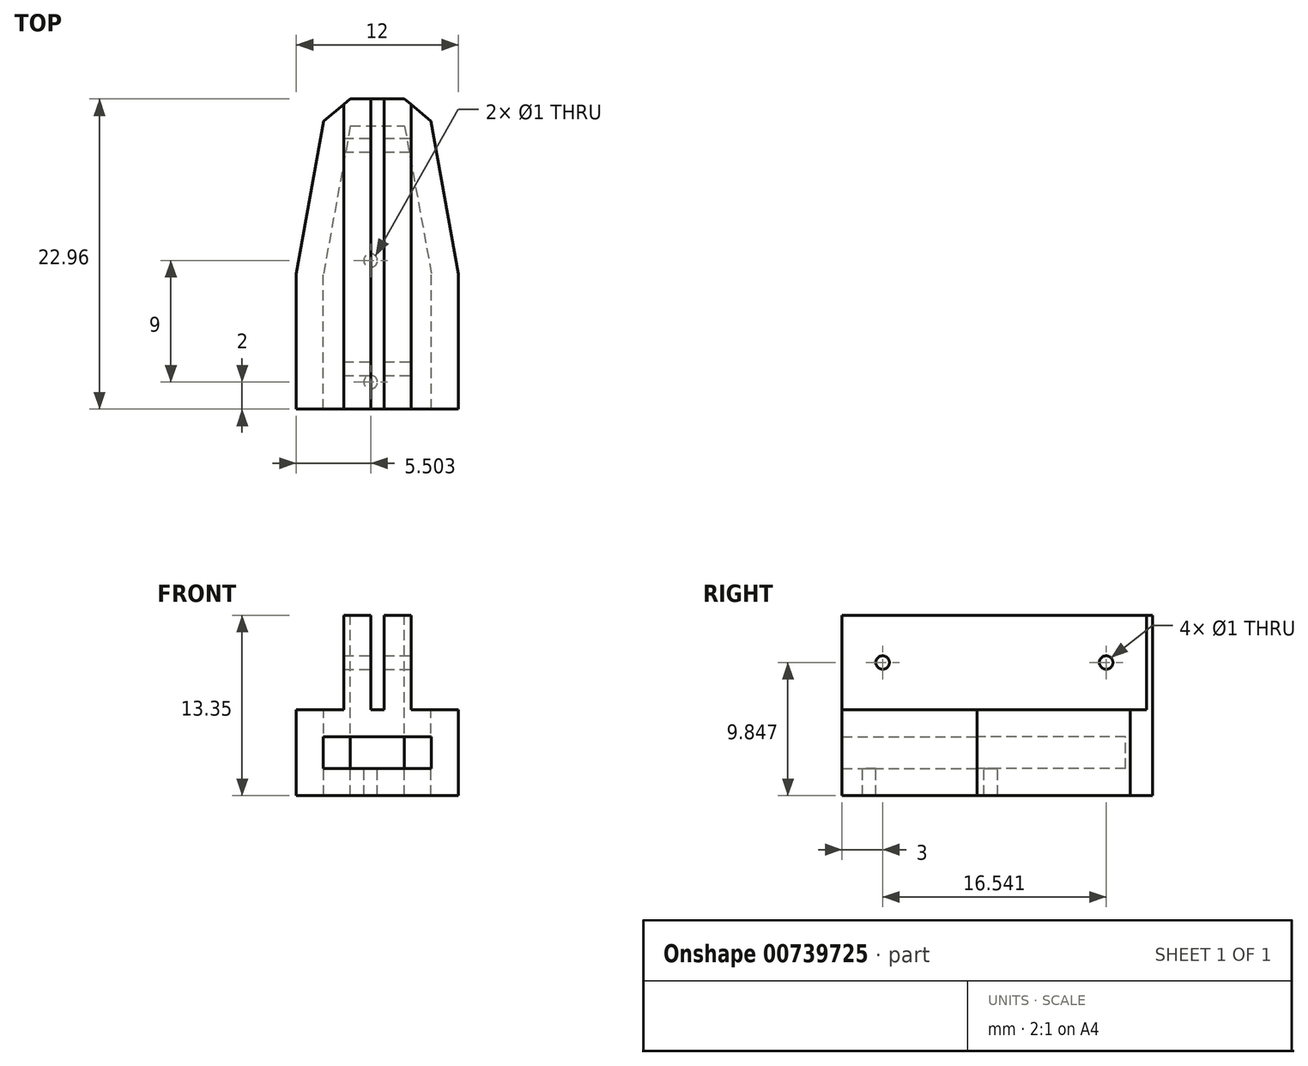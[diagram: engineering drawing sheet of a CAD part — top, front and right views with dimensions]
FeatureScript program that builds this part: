
annotation { "Feature Type Name" : "Feature", "Feature Type Description" : "" }
export const myFeature = defineFeature(function(context is Context, id is Id, definition is map)
    precondition{}
    {
        {
            var Q0;
            Q0=qCreatedBy(makeId("Top.planeOp"),FACE);
            var sketch = newSketch(context, id + "F0", { "sketchPlane" : qUnion([Q0])});
            skLineSegment(sketch, "E0", {"start": v(-17.89, 0) * mm, "end": v(-9.89, 0) * mm});
            skLineSegment(sketch, "E1", {"start": v(-17.89, 0) * mm, "end": v(-17.89, 10) * mm});
            skLineSegment(sketch, "E2", {"start": v(-9.89, 0) * mm, "end": v(-9.89, 10) * mm});
            skLineSegment(sketch, "E3", {"start": v(-11.89, 20.96) * mm, "end": v(-9.89, 10) * mm});
            skLineSegment(sketch, "E4", {"start": v(-15.89, 20.96) * mm, "end": v(-11.89, 20.96) * mm});
            skLineSegment(sketch, "E5", {"start": v(-15.89, 20.96) * mm, "end": v(-17.89, 10) * mm});
            skLineSegment(sketch, "E6", {"start": v(-17.89, 0) * mm, "end": v(-19.89, 0) * mm});
            skLineSegment(sketch, "E7", {"start": v(-17.89, 10) * mm, "end": v(-19.89, 10) * mm});
            skLineSegment(sketch, "E8", {"start": v(-15.89, 20.96) * mm, "end": v(-17.86, 21.32) * mm});
            skLineSegment(sketch, "E9", {"start": v(-11.89, 20.96) * mm, "end": v(-11.89, 22.96) * mm});
            skLineSegment(sketch, "E10", {"start": v(-11.89, 20.96) * mm, "end": v(-9.92, 21.32) * mm});
            skLineSegment(sketch, "E11", {"start": v(-9.89, 0) * mm, "end": v(-7.89, 0) * mm});
            skLineSegment(sketch, "E12", {"start": v(-15.89, 20.96) * mm, "end": v(-15.89, 22.96) * mm});
            skLineSegment(sketch, "E13", {"start": v(-9.89, 10) * mm, "end": v(-7.89, 10) * mm});
            skLineSegment(sketch, "E14", {"start": v(-19.89, 10) * mm, "end": v(-19.89, 0) * mm});
            skLineSegment(sketch, "E15", {"start": v(-17.86, 21.32) * mm, "end": v(-19.89, 10) * mm});
            skLineSegment(sketch, "E16", {"start": v(-17.86, 21.32) * mm, "end": v(-15.89, 22.96) * mm});
            skLineSegment(sketch, "E17", {"start": v(-11.89, 22.96) * mm, "end": v(-15.89, 22.96) * mm});
            skLineSegment(sketch, "E18", {"start": v(-11.89, 22.96) * mm, "end": v(-9.92, 21.32) * mm});
            skLineSegment(sketch, "E19", {"start": v(-9.92, 21.32) * mm, "end": v(-7.89, 10) * mm});
            skLineSegment(sketch, "E20", {"start": v(-7.89, 10) * mm, "end": v(-7.89, 0) * mm});
            skLineSegment(sketch, "E21", {"start": v(-13.89, 20.96) * mm, "end": v(-13.89, 0) * mm});
            skSolve(sketch);
        }
        {
            var Q0;
            Q0=makeQuery(id+"F0.imprint","IMPRINT",FACE,{"disambiguationData":[TD([[makeQuery(id+"F0.imprint","IMPRINT",EDGE,{"derivedFrom":sQuery(id+"F0.wireOp",EDGE,"E1")}),1.0]])]});
            var Q1;
            Q1=makeQuery(id+"F0.imprint","IMPRINT",FACE,{"disambiguationData":[TD([[makeQuery(id+"F0.imprint","IMPRINT",EDGE,{"derivedFrom":sQuery(id+"F0.wireOp",EDGE,"E2")}),-1.0]])]});
            var Q2;
            Q2=makeQuery(id+"F0.imprint","IMPRINT",FACE,{"disambiguationData":[TD([[makeQuery(id+"F0.imprint","IMPRINT",EDGE,{"derivedFrom":sQuery(id+"F0.wireOp",EDGE,"E8")}),-1.0]])]});
            var Q3;
            Q3=makeQuery(id+"F0.imprint","IMPRINT",FACE,{"disambiguationData":[TD([[makeQuery(id+"F0.imprint","IMPRINT",EDGE,{"derivedFrom":sQuery(id+"F0.wireOp",EDGE,"E9")}),-1.0]])]});
            var Q4;
            Q4=makeQuery(id+"F0.imprint","IMPRINT",FACE,{"disambiguationData":[TD([[makeQuery(id+"F0.imprint","IMPRINT",EDGE,{"derivedFrom":sQuery(id+"F0.wireOp",EDGE,"E3")}),1.0]])]});
            var Q5;
            Q5=makeQuery(id+"F0.imprint","IMPRINT",FACE,{"disambiguationData":[TD([[makeQuery(id+"F0.imprint","IMPRINT",EDGE,{"derivedFrom":sQuery(id+"F0.wireOp",EDGE,"E4")}),1.0]])]});
            var Q6;
            Q6=makeQuery(id+"F0.imprint","IMPRINT",FACE,{"disambiguationData":[TD([[makeQuery(id+"F0.imprint","IMPRINT",EDGE,{"derivedFrom":sQuery(id+"F0.wireOp",EDGE,"E5")}),-1.0]])]});
            extrude(context, id + "F1", {"entities" : qUnion([Q0, Q1, Q2, Q3, Q4, Q5, Q6]), "depth" : -2.34 * mm, "offsetDistance" : 25.4 * mm});
        }
        {
            var Q0;
            Q0 = qSketchRegion(id + "F0", true);
            var Q1;
            Q1=makeQuery(id+"F0.imprint","IMPRINT",FACE,{"disambiguationData":[TD([[makeQuery(id+"F0.imprint","IMPRINT",EDGE,{"derivedFrom":sQuery(id+"F0.wireOp",EDGE,"Zf4kV3ub-T76P-5IQD-aEpu-UKvpmo5hTW54")}),-1.0]])]});
            extrude(context, id + "F2", {"entities" : qUnion([Q0, Q1]), "operationType" : NewBodyOperationType.ADD, "depth" : 2 * mm, "offsetDistance" : 25.4 * mm});
        }
        {
            var Q0;
            Q0=makeQuery(id+"F1.opExtrude","CAP_FACE",FACE,{"disambiguationData":[OSD([sQuery(id+"F0.wireOp",EDGE,"E1"),sQuery(id+"F0.wireOp",EDGE,"E2"),sQuery(id+"F0.wireOp",EDGE,"E3"),sQuery(id+"F0.wireOp",EDGE,"E4"),sQuery(id+"F0.wireOp",EDGE,"E5"),sQuery(id+"F0.wireOp",EDGE,"E6"),sQuery(id+"F0.wireOp",EDGE,"E11"),sQuery(id+"F0.wireOp",EDGE,"E14"),sQuery(id+"F0.wireOp",EDGE,"E15"),sQuery(id+"F0.wireOp",EDGE,"E16"),sQuery(id+"F0.wireOp",EDGE,"E17"),sQuery(id+"F0.wireOp",EDGE,"E18"),sQuery(id+"F0.wireOp",EDGE,"E19"),sQuery(id+"F0.wireOp",EDGE,"E20")])],"isStart":false});
            var sketch = newSketch(context, id + "F3", { "sketchPlane" : qUnion([Q0])});
            skLineSegment(sketch, "E22", {"start": v(-19.89, 0) * mm, "end": v(-7.89, 0) * mm});
            skLineSegment(sketch, "E23", {"start": v(-7.89, 0) * mm, "end": v(-7.89, -10) * mm});
            skLineSegment(sketch, "E24", {"start": v(-7.89, -10) * mm, "end": v(-9.92, -21.32) * mm});
            skLineSegment(sketch, "E25", {"start": v(-9.92, -21.32) * mm, "end": v(-11.89, -22.96) * mm});
            skLineSegment(sketch, "E26", {"start": v(-11.89, -22.96) * mm, "end": v(-15.89, -22.96) * mm});
            skLineSegment(sketch, "E27", {"start": v(-15.89, -22.96) * mm, "end": v(-17.86, -21.32) * mm});
            skLineSegment(sketch, "E28", {"start": v(-17.86, -21.32) * mm, "end": v(-19.89, -10) * mm});
            skLineSegment(sketch, "E29", {"start": v(-17.89, 0) * mm, "end": v(-14.39, 0) * mm});
            skLineSegment(sketch, "E30", {"start": v(-14.39, 0) * mm, "end": v(-14.39, -2) * mm});
            skCircle(sketch, "E31", {"center": v(-14.39, -2) * mm, "radius": 0.5 * mm});
            skLineSegment(sketch, "E32", {"start": v(-14.39, -2) * mm, "end": v(-14.39, -11) * mm});
            skCircle(sketch, "E33", {"center": v(-14.39, -11) * mm, "radius": 0.5 * mm});
            skSolve(sketch);
        }
        {
            var Q0;
            {var subQ1=makeQuery(id+"F1.opExtrude","CAP_EDGE",EDGE,{"disambiguationData":[OSD([sQuery(id+"F0.wireOp",EDGE,"E1")])],"isStart":false});Q0=makeQuery(id+"F3.imprint","IMPRINT",FACE,{"disambiguationData":[TD([[makeQuery(id+"F3.imprint","IMPRINT",EDGE,{"derivedFrom":subQ1}),1.0]])]});}
            var Q1;
            {var subQ4=sQuery(id+"F3.wireOp",EDGE,"E23");Q1=makeQuery(id+"F3.imprint","IMPRINT",FACE,{"disambiguationData":[TD([[makeQuery(id+"F3.imprint","IMPRINT",EDGE,{"derivedFrom":subQ4}),1.0]])]});}
            extrude(context, id + "F4", {"entities" : qUnion([Q0, Q1]), "operationType" : NewBodyOperationType.ADD, "depth" : 2 * mm, "offsetDistance" : 25.4 * mm});
        }
        {
            var Q0;
            Q0=makeQuery(id+"F2.opExtrude","CAP_FACE",FACE,{"disambiguationData":[OSD([sQuery(id+"F0.wireOp",EDGE,"E0"),sQuery(id+"F0.wireOp",EDGE,"E6"),sQuery(id+"F0.wireOp",EDGE,"E11"),sQuery(id+"F0.wireOp",EDGE,"E14"),sQuery(id+"F0.wireOp",EDGE,"E15"),sQuery(id+"F0.wireOp",EDGE,"E16"),sQuery(id+"F0.wireOp",EDGE,"E17"),sQuery(id+"F0.wireOp",EDGE,"E18"),sQuery(id+"F0.wireOp",EDGE,"E19"),sQuery(id+"F0.wireOp",EDGE,"E20")])],"isStart":false});
            var sketch = newSketch(context, id + "F5", { "sketchPlane" : qUnion([Q0])});
            skLineSegment(sketch, "E34", {"start": v(-13.89, 0) * mm, "end": v(-13.39, 0) * mm});
            skLineSegment(sketch, "E35", {"start": v(-13.39, 0) * mm, "end": v(-11.39, 0) * mm});
            skLineSegment(sketch, "E36", {"start": v(-13.89, 0) * mm, "end": v(-14.39, 0) * mm});
            skLineSegment(sketch, "E37", {"start": v(-14.39, 0) * mm, "end": v(-16.39, 0) * mm});
            skLineSegment(sketch, "E38", {"start": v(-14.39, 0) * mm, "end": v(-14.39, 22.96) * mm});
            skLineSegment(sketch, "E39", {"start": v(-13.39, 0) * mm, "end": v(-13.39, 22.96) * mm});
            skLineSegment(sketch, "E40", {"start": v(-11.39, 0) * mm, "end": v(-11.39, 22.54) * mm});
            skLineSegment(sketch, "E41", {"start": v(-16.39, 0) * mm, "end": v(-16.39, 22.54) * mm});
            skLineSegment(sketch, "E42", {"start": v(-16.39, 22.54) * mm, "end": v(-15.89, 22.96) * mm});
            skLineSegment(sketch, "E43", {"start": v(-15.89, 22.96) * mm, "end": v(-14.39, 22.96) * mm});
            skLineSegment(sketch, "E44", {"start": v(-11.39, 22.54) * mm, "end": v(-11.89, 22.96) * mm});
            skLineSegment(sketch, "E45", {"start": v(-11.89, 22.96) * mm, "end": v(-13.39, 22.96) * mm});
            skSolve(sketch);
        }
        {
            var Q0;
            Q0 = qSketchRegion(id + "F5", true);
            extrude(context, id + "F6", {"entities" : qUnion([Q0]), "operationType" : NewBodyOperationType.ADD, "depth" : 7 * mm, "offsetDistance" : 25.4 * mm});
        }
        {
            var Q0;
            Q0=makeQuery(id+"F6.opExtrude","SWEPT_FACE",FACE,{"disambiguationData":[OSD([sQuery(id+"F5.wireOp",EDGE,"E40")])]});
            var sketch = newSketch(context, id + "F7", { "sketchPlane" : qUnion([Q0])});
            skCircle(sketch, "E46", {"center": v(3, 5.5) * mm, "radius": 0.5 * mm});
            skCircle(sketch, "E47", {"center": v(19.54, 5.5) * mm, "radius": 0.5 * mm});
            skLineSegment(sketch, "E48", {"start": v(0, 9) * mm, "end": v(0, 5.5) * mm});
            skLineSegment(sketch, "E49", {"start": v(22.54, 5.5) * mm, "end": v(0, 5.5) * mm});
            skLineSegment(sketch, "E50", {"start": v(0, 5.5) * mm, "end": v(3, 5.5) * mm});
            skLineSegment(sketch, "E51", {"start": v(22.54, 5.5) * mm, "end": v(19.54, 5.5) * mm});
            skSolve(sketch);
        }
        {
            var Q0;
            Q0=sQuery(id+"F7.wireOp",VERTEX,"E46.center");
            var Q1;
            Q1=sQuery(id+"F7.wireOp",VERTEX,"E47.center");
            var Q2;
            Q2=makeQuery(id+"F1.opExtrude","SWEPT_BODY",BODY,{"disambiguationData":[OSD([sQuery(id+"F0.wireOp",EDGE,"E1"),sQuery(id+"F0.wireOp",EDGE,"E2"),sQuery(id+"F0.wireOp",EDGE,"E3"),sQuery(id+"F0.wireOp",EDGE,"E4"),sQuery(id+"F0.wireOp",EDGE,"E5"),sQuery(id+"F0.wireOp",EDGE,"E6"),sQuery(id+"F0.wireOp",EDGE,"E11"),sQuery(id+"F0.wireOp",EDGE,"E14"),sQuery(id+"F0.wireOp",EDGE,"E15"),sQuery(id+"F0.wireOp",EDGE,"E16"),sQuery(id+"F0.wireOp",EDGE,"E17"),sQuery(id+"F0.wireOp",EDGE,"E18"),sQuery(id+"F0.wireOp",EDGE,"E19"),sQuery(id+"F0.wireOp",EDGE,"E20")])]});
            hole(context, id + "F8", {"style" : HoleStyle.SIMPLE, "endStyle" : HoleEndStyle.THROUGH, "holeDiameter" : 1 * mm, "majorDiameter" : 6.35 * mm, "isTappedThrough" : true, "tappedDepth" : 12.7 * mm, "tapClearance" : 3, "locations" : qUnion([Q0, Q1]), "scope" : qUnion([Q2])});
        }
    });
